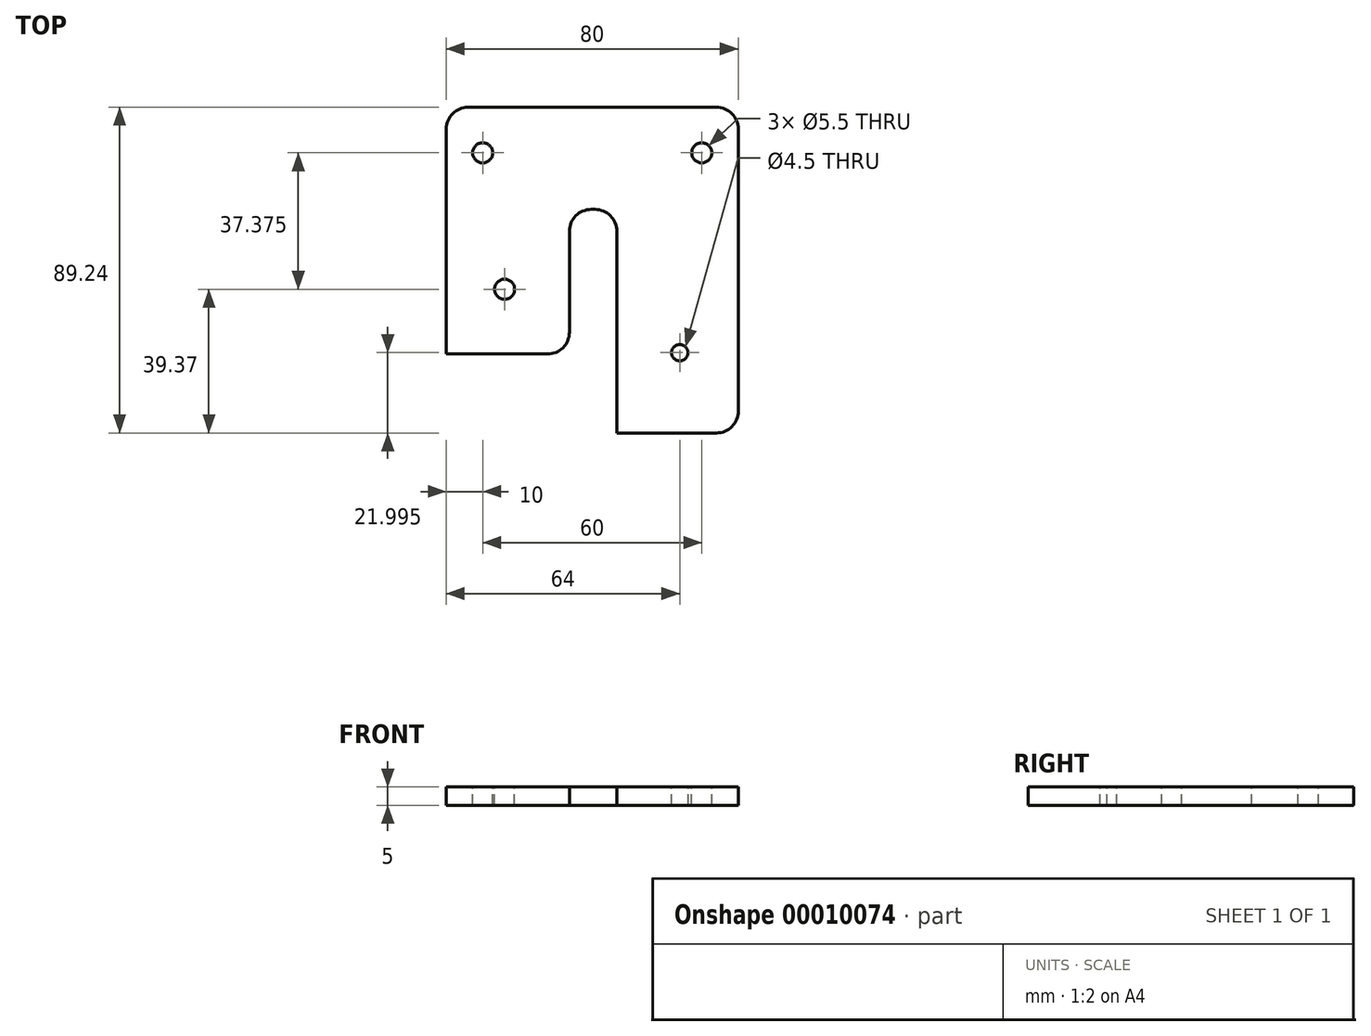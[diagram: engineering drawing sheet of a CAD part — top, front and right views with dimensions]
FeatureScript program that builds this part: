
annotation { "Feature Type Name" : "Feature", "Feature Type Description" : "" }
export const myFeature = defineFeature(function(context is Context, id is Id, definition is map)
    precondition{}
    {
        {
            var Q0;
            Q0=qCreatedBy(makeId("Top.planeOp"),FACE);
            var sketch = newSketch(context, id + "F0", { "sketchPlane" : qUnion([Q0])});
            skLineSegment(sketch, "E0.rect.bottom", {"start": v(-40, 44.62) * mm, "end": v(40, 44.62) * mm});
            skLineSegment(sketch, "E0.rect.top", {"start": v(-40, -44.62) * mm, "end": v(40, -44.62) * mm});
            skLineSegment(sketch, "E0.rect.left", {"start": v(-40, 44.62) * mm, "end": v(-40, -44.62) * mm});
            skLineSegment(sketch, "E0.rect.right", {"start": v(40, 44.62) * mm, "end": v(40, -44.62) * mm});
            skPoint(sketch, "E0.rect.middle", {"position": v(0, 0) * mm});
            skSolve(sketch);
        }
        {
            var Q0;
            Q0=qSketchRegion(id+"F0",true);
            extrude(context, id + "F1", {"entities" : qUnion([Q0]), "depth" : 5 * mm});
        }
        {
            var Q0;
            Q0=makeQuery(id+"F1.opExtrude","CAP_FACE",FACE,{"disambiguationData":[OSD([sQuery(id+"F0.wireOp",EDGE,"E0.rect.bottom"),sQuery(id+"F0.wireOp",EDGE,"E0.rect.top"),sQuery(id+"F0.wireOp",EDGE,"E0.rect.left"),sQuery(id+"F0.wireOp",EDGE,"E0.rect.right")])],"isStart":false});
            var sketch = newSketch(context, id + "F2", { "sketchPlane" : qUnion([Q0])});
            skCircle(sketch, "E1", {"center": v(-24, -5.25) * mm, "radius": 2.75 * mm});
            skCircle(sketch, "E2", {"center": v(24, -22.63) * mm, "radius": 2.25 * mm});
            skCircle(sketch, "E3", {"center": v(-30, 32.12) * mm, "radius": 2.75 * mm});
            skCircle(sketch, "E4", {"center": v(30, 32.12) * mm, "radius": 2.75 * mm});
            skSolve(sketch);
        }
        {
            var Q0;
            Q0=qSketchRegion(id+"F2",true);
            extrude(context, id + "F3", {"entities" : qUnion([Q0]), "operationType" : NewBodyOperationType.REMOVE, "endBound" : BoundingType.THROUGH_ALL, "oppositeDirection" : true, "depth" : 25 * mm});
        }
        {
            var Q0;
            Q0=makeQuery(id+"F1.opExtrude","CAP_FACE",FACE,{"disambiguationData":[OSD([sQuery(id+"F0.wireOp",EDGE,"E0.rect.bottom"),sQuery(id+"F0.wireOp",EDGE,"E0.rect.top"),sQuery(id+"F0.wireOp",EDGE,"E0.rect.left"),sQuery(id+"F0.wireOp",EDGE,"E0.rect.right")])],"isStart":false});
            var sketch = newSketch(context, id + "F4", { "sketchPlane" : qUnion([Q0])});
            skLineSegment(sketch, "E5", {"start": v(-40, -23) * mm, "end": v(-6.25, -23) * mm});
            skLineSegment(sketch, "E6", {"start": v(-6.25, -23) * mm, "end": v(-6.25, 16.62) * mm});
            skLineSegment(sketch, "E7", {"start": v(-6.25, 16.62) * mm, "end": v(6.75, 16.62) * mm});
            skLineSegment(sketch, "E8", {"start": v(6.75, 16.62) * mm, "end": v(6.75, -44.62) * mm});
            skLineSegment(sketch, "E9", {"start": v(6.75, -44.62) * mm, "end": v(-40, -44.62) * mm});
            skLineSegment(sketch, "E10", {"start": v(-40, -44.62) * mm, "end": v(-40, -23) * mm});
            skSolve(sketch);
        }
        {
            var Q0;
            Q0=qSketchRegion(id+"F4",true);
            extrude(context, id + "F5", {"entities" : qUnion([Q0]), "operationType" : NewBodyOperationType.REMOVE, "endBound" : BoundingType.THROUGH_ALL, "oppositeDirection" : true, "depth" : 25 * mm});
        }
        {
            var Q0;
            Q0=makeQuery(id+"F5.boolean.opBoolean","COPY",EDGE,{"derivedFrom":makeQuery(id+"F5.opExtrude","SWEPT_EDGE",EDGE,{"disambiguationData":[OSD([sQuery(id+"F0.wireOp",EDGE,"E0.rect.left"),sQuery(id+"F4.wireOp",EDGE,"E5"),sQuery(id+"F4.wireOp",EDGE,"E10")])]})});
            var Q1;
            Q1=makeQuery(id+"F5.boolean.opBoolean","COPY",EDGE,{"derivedFrom":makeQuery(id+"F5.opExtrude","SWEPT_EDGE",EDGE,{"disambiguationData":[OSD([sQuery(id+"F4.wireOp",EDGE,"E5"),sQuery(id+"F4.wireOp",EDGE,"E6")])]})});
            var Q2;
            Q2=makeQuery(id+"F5.boolean.opBoolean","COPY",EDGE,{"derivedFrom":makeQuery(id+"F5.opExtrude","SWEPT_EDGE",EDGE,{"disambiguationData":[OSD([sQuery(id+"F4.wireOp",EDGE,"E6"),sQuery(id+"F4.wireOp",EDGE,"E7")])]})});
            var Q3;
            Q3=makeQuery(id+"F5.boolean.opBoolean","COPY",EDGE,{"derivedFrom":makeQuery(id+"F5.opExtrude","SWEPT_EDGE",EDGE,{"disambiguationData":[OSD([sQuery(id+"F0.wireOp",EDGE,"E0.rect.top"),sQuery(id+"F4.wireOp",EDGE,"E8"),sQuery(id+"F4.wireOp",EDGE,"E9")])]})});
            var Q4;
            Q4=makeQuery(id+"F1.opExtrude","SWEPT_EDGE",EDGE,{"disambiguationData":[OSD([sQuery(id+"F0.wireOp",EDGE,"E0.rect.top"),sQuery(id+"F0.wireOp",EDGE,"E0.rect.right")])]});
            var Q5;
            Q5=makeQuery(id+"F1.opExtrude","SWEPT_EDGE",EDGE,{"disambiguationData":[OSD([sQuery(id+"F0.wireOp",EDGE,"E0.rect.bottom"),sQuery(id+"F0.wireOp",EDGE,"E0.rect.right")])]});
            var Q6;
            Q6=makeQuery(id+"F5.boolean.opBoolean","COPY",EDGE,{"derivedFrom":makeQuery(id+"F5.opExtrude","SWEPT_EDGE",EDGE,{"disambiguationData":[OSD([sQuery(id+"F4.wireOp",EDGE,"E7"),sQuery(id+"F4.wireOp",EDGE,"E8")])]})});
            var Q7;
            Q7=makeQuery(id+"F1.opExtrude","SWEPT_EDGE",EDGE,{"disambiguationData":[OSD([sQuery(id+"F0.wireOp",EDGE,"E0.rect.bottom"),sQuery(id+"F0.wireOp",EDGE,"E0.rect.left")])]});
            fillet(context, id + "F6", {"entities" : qUnion([Q0, Q1, Q2, Q3, Q4, Q5, Q6, Q7]), "radius" : 6 * mm, "tangentPropagation" : true, "allowEdgeOverflow" : false});
        }
    });
